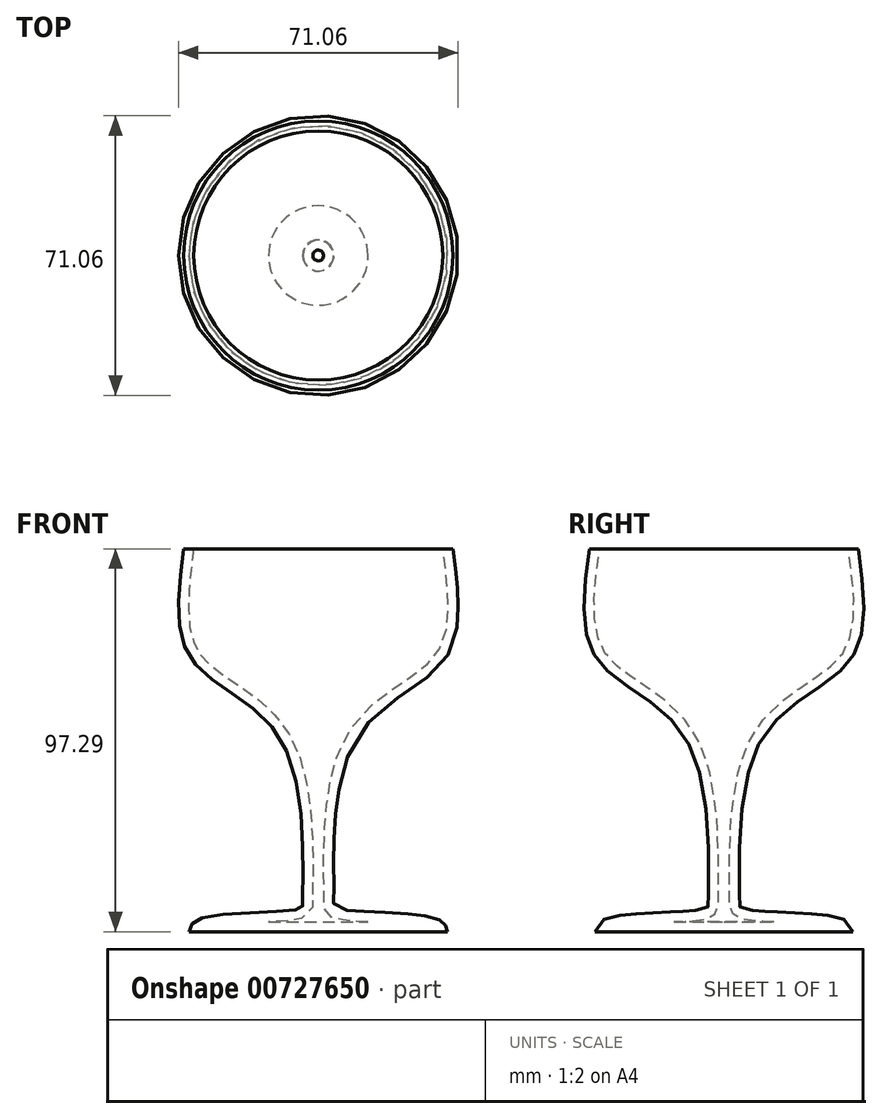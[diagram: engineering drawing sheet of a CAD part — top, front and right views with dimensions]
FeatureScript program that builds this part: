
annotation { "Feature Type Name" : "Feature", "Feature Type Description" : "" }
export const myFeature = defineFeature(function(context is Context, id is Id, definition is map)
    precondition{}
    {
        {
            var Q0;
            Q0=qCreatedBy(makeId("Front.planeOp"),FACE);
            var sketch = newSketch(context, id + "F0", { "sketchPlane" : qUnion([Q0])});
            skFitSpline(sketch, "E0", {"points": [v(-36.4, 55.24) * mm, v(-34.3, 27.1) * mm, v(-11.28, 6.16) * mm, v(-6.16, -33.84) * mm, v(-7.1, -36.17) * mm, v(-32.45, -38.73) * mm, v(-35, -41.98) * mm], "startDerivative": vector(-20.55, -155.58) * mm, "endDerivative": vector(-8.98, -46.71) * mm});
            skLineSegment(sketch, "E1", {"start": v(-35, -41.98) * mm, "end": v(-2.2, -41.98) * mm});
            skLineSegment(sketch, "E2", {"start": v(-2.2, -41.98) * mm, "end": v(-2.2, 56.17) * mm});
            skLineSegment(sketch, "E3", {"start": v(-2.2, 56.17) * mm, "end": v(-36.4, 55.24) * mm});
            skSolve(sketch);
        }
        {
            var Q0;
            Q0=makeQuery(id+"F0.imprint","IMPRINT",FACE,{"disambiguationData":[TD([[makeQuery(id+"F0.imprint","IMPRINT",EDGE,{"derivedFrom":sQuery(id+"F0.wireOp",EDGE,"E0")}),1.0]])]});
            var Q1;
            Q1=sQuery(id+"F0.wireOp",EDGE,"E2");
            revolve(context, id + "F1", {"surfaceOperationType" : NewSurfaceOperationType.NEW, "entities" : qUnion([Q0]), "axis" : qUnion([Q1]), "revolveType" : RevolveType.FULL});
        }
        {
            var Q0;
            Q0=makeQuery(id+"F1.opRevolve","SWEPT_FACE",FACE,{"disambiguationData":[OSD([sQuery(id+"F0.wireOp",EDGE,"E3")])]});
            shell(context, id + "F2", {"entities" : qUnion([Q0]), "thickness" : 2.54 * mm});
        }
    });
